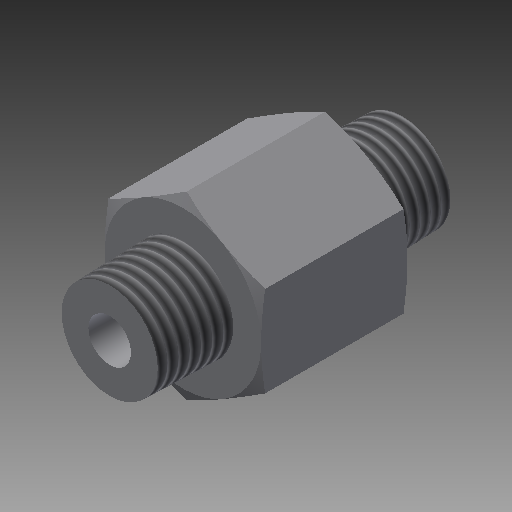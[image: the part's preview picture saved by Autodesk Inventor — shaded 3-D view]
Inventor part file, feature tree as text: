
AUTODESK INVENTOR PART (.ipt)
format: ipt  version: 2017 (Build 210142000, 142)  size: 175,616 bytes
history: native  units: in
note: dims shown in document units (in); Inventor stores cm internally (conversion verified against a paired STEP export)
features: sketch x4, extrude x3, plane x2, thread x2, other x1, hole x1, revolve x1, mirror x1, reference x1
ambient origin geometry x8: Origin, YZ Plane, XZ Plane, XY Plane, X Axis, Y Axis, Z Axis, Center Point
bodies: Solid1 (feature_tree)
feature tree (16):
  sketch  "Sketch1"  dims[d2=0.5in d3=0.0in d20=0.25in d21=-0.0123in]
  extrude  "Extrusion1"  Depth=0.25in
  plane  "Work Plane1"
  other  "Work Axis3"
  extrude  "Extrusion3"  Depth=0.25in
  thread  "Thread2"  [1 undecoded]
  hole  "Hole2"  [1 undecoded]
  extrude  "Extrusion4"  Depth=0.0414in
  thread  "Thread3"  [1 undecoded]
  revolve  "Revolution3"  [1 undecoded]
  plane  "Work Plane4"
  mirror  "Mirror4"
  sketch  "Sketch6"  dims[d22=0.392in d23=0.0in]
  reference  "Reference3"
  sketch  "Sketch7"  dims[d24=0.13in d25=0.75in d26=0.375in d27=0.25in d28=0.5635in d29=1.0in d30=0.8108in d31=0.25in d32=-0.0123in d33=0.392in d34=0.0in]
  sketch  "Sketch8"  dims[d35=90.0deg d36=0.5355in d37=0.0414in d38=0.0415in]
note: 4 required parameter values undecoded (feature->parameter linkage not recoverable at this tier; creation-order binding heuristic only, values carry confidence <= 0.55)
